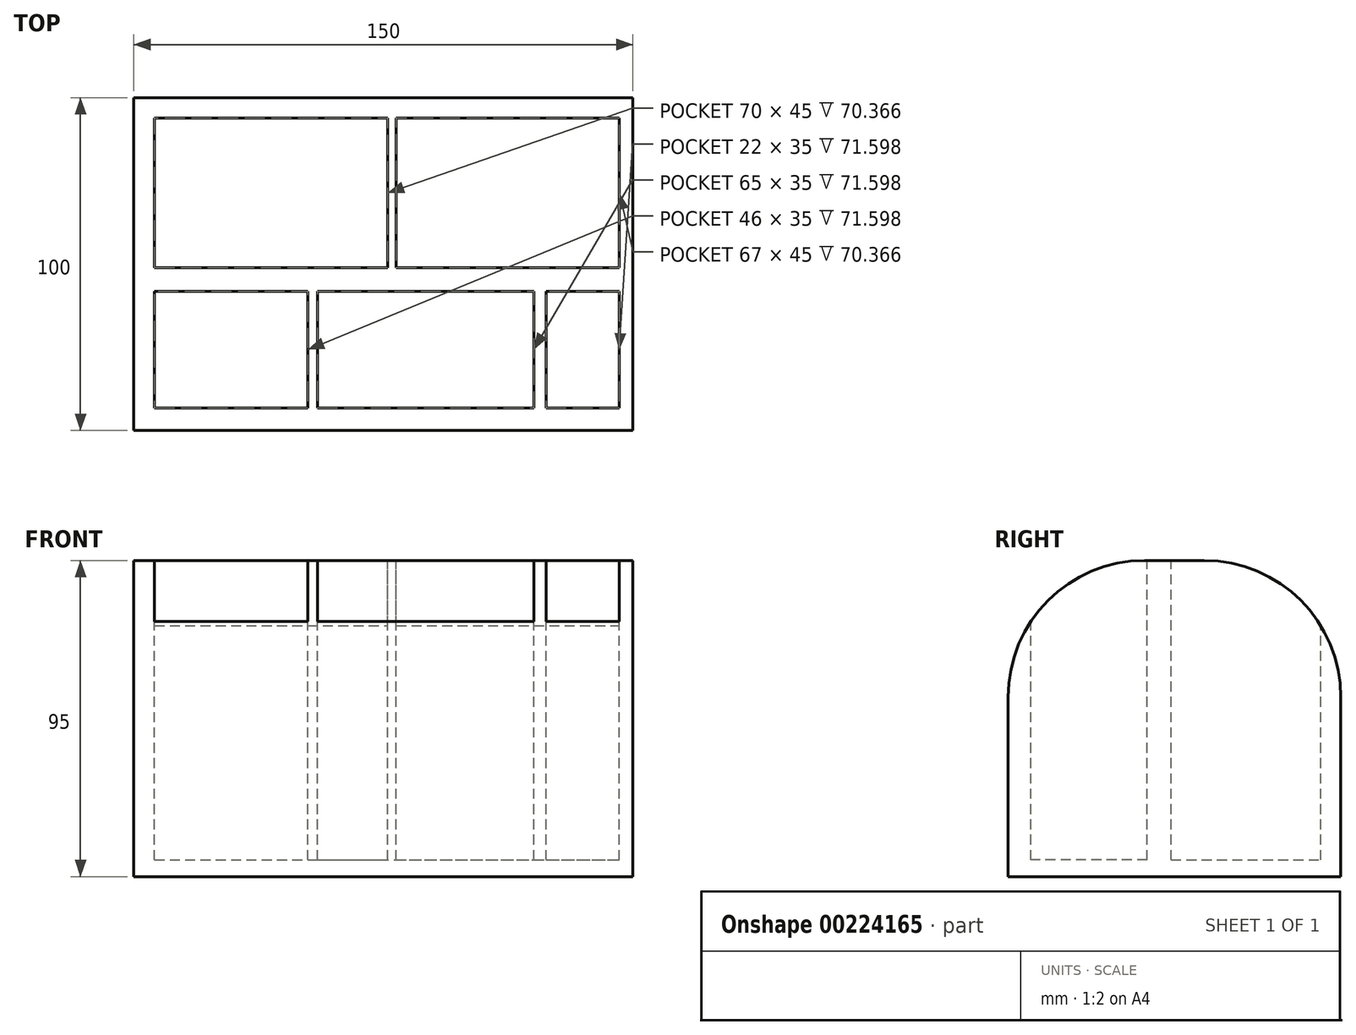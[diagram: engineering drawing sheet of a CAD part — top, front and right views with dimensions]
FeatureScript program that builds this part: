
annotation { "Feature Type Name" : "Feature", "Feature Type Description" : "" }
export const myFeature = defineFeature(function(context is Context, id is Id, definition is map)
    precondition{}
    {
        {
            var Q0;
            Q0=qCreatedBy(makeId("Top.planeOp"),FACE);
            var sketch = newSketch(context, id + "F0", { "sketchPlane" : qUnion([Q0])});
            skLineSegment(sketch, "E0.bottom", {"start": v(-52.23, 53.64) * mm, "end": v(97.77, 53.64) * mm});
            skLineSegment(sketch, "E0.top", {"start": v(-52.23, -46.36) * mm, "end": v(97.77, -46.36) * mm});
            skLineSegment(sketch, "E0.left", {"start": v(-52.23, 53.64) * mm, "end": v(-52.23, -46.36) * mm});
            skLineSegment(sketch, "E0.right", {"start": v(97.77, 53.64) * mm, "end": v(97.77, -46.36) * mm});
            skSolve(sketch);
        }
        {
            var Q0;
            Q0=makeQuery(id+"F0.imprint","IMPRINT",FACE,{"disambiguationData":[TD([[makeQuery(id+"F0.imprint","IMPRINT",EDGE,{"derivedFrom":sQuery(id+"F0.wireOp",EDGE,"E0.bottom")}),-1.0]])]});
            extrude(context, id + "F1", {"entities" : qUnion([Q0]), "depth" : 95 * mm});
        }
        {
            var Q0;
            Q0=makeQuery(id+"F1.opExtrude","CAP_FACE",FACE,{"disambiguationData":[OSD([sQuery(id+"F0.wireOp",EDGE,"E0.bottom"),sQuery(id+"F0.wireOp",EDGE,"E0.top"),sQuery(id+"F0.wireOp",EDGE,"E0.left"),sQuery(id+"F0.wireOp",EDGE,"E0.right")])],"isStart":false});
            var sketch = newSketch(context, id + "F2", { "sketchPlane" : qUnion([Q0])});
            skLineSegment(sketch, "E1.bottom", {"start": v(-46, -39.55) * mm, "end": v(0, -39.55) * mm});
            skLineSegment(sketch, "E1.top", {"start": v(-46, -4.55) * mm, "end": v(0, -4.55) * mm});
            skLineSegment(sketch, "E1.left", {"start": v(-46, -39.55) * mm, "end": v(-46, -4.55) * mm});
            skLineSegment(sketch, "E1.right", {"start": v(0, -39.55) * mm, "end": v(0, -4.55) * mm});
            skLineSegment(sketch, "E2.bottom", {"start": v(2.94, -4.55) * mm, "end": v(67.94, -4.55) * mm});
            skLineSegment(sketch, "E2.top", {"start": v(2.94, -39.55) * mm, "end": v(67.94, -39.55) * mm});
            skLineSegment(sketch, "E2.left", {"start": v(2.94, -4.55) * mm, "end": v(2.94, -39.55) * mm});
            skLineSegment(sketch, "E2.right", {"start": v(67.94, -4.55) * mm, "end": v(67.94, -39.55) * mm});
            skLineSegment(sketch, "E3.bottom", {"start": v(71.64, -4.55) * mm, "end": v(93.64, -4.55) * mm});
            skLineSegment(sketch, "E3.top", {"start": v(71.64, -39.55) * mm, "end": v(93.64, -39.55) * mm});
            skLineSegment(sketch, "E3.left", {"start": v(71.64, -4.55) * mm, "end": v(71.64, -39.55) * mm});
            skLineSegment(sketch, "E3.right", {"start": v(93.64, -4.55) * mm, "end": v(93.64, -39.55) * mm});
            skLineSegment(sketch, "E4.bottom", {"start": v(-46, 2.62) * mm, "end": v(24, 2.62) * mm});
            skLineSegment(sketch, "E4.top", {"start": v(-46, 47.62) * mm, "end": v(24, 47.62) * mm});
            skLineSegment(sketch, "E4.left", {"start": v(-46, 2.62) * mm, "end": v(-46, 47.62) * mm});
            skLineSegment(sketch, "E4.right", {"start": v(24, 2.62) * mm, "end": v(24, 47.62) * mm});
            skLineSegment(sketch, "E5.bottom", {"start": v(26.64, 2.62) * mm, "end": v(93.64, 2.62) * mm});
            skLineSegment(sketch, "E5.top", {"start": v(26.64, 47.62) * mm, "end": v(93.64, 47.62) * mm});
            skLineSegment(sketch, "E5.left", {"start": v(26.64, 2.62) * mm, "end": v(26.64, 47.62) * mm});
            skLineSegment(sketch, "E5.right", {"start": v(93.64, 2.62) * mm, "end": v(93.64, 47.62) * mm});
            skSolve(sketch);
        }
        {
            var Q0;
            Q0=makeQuery(id+"F2.imprint","IMPRINT",FACE,{"disambiguationData":[TD([[makeQuery(id+"F2.imprint","IMPRINT",EDGE,{"derivedFrom":sQuery(id+"F2.wireOp",EDGE,"E4.bottom")}),1.0]])]});
            var Q1;
            Q1=makeQuery(id+"F2.imprint","IMPRINT",FACE,{"disambiguationData":[TD([[makeQuery(id+"F2.imprint","IMPRINT",EDGE,{"derivedFrom":sQuery(id+"F2.wireOp",EDGE,"E5.bottom")}),1.0]])]});
            var Q2;
            Q2=makeQuery(id+"F2.imprint","IMPRINT",FACE,{"disambiguationData":[TD([[makeQuery(id+"F2.imprint","IMPRINT",EDGE,{"derivedFrom":sQuery(id+"F2.wireOp",EDGE,"E1.bottom")}),1.0]])]});
            var Q3;
            Q3=makeQuery(id+"F2.imprint","IMPRINT",FACE,{"disambiguationData":[TD([[makeQuery(id+"F2.imprint","IMPRINT",EDGE,{"derivedFrom":sQuery(id+"F2.wireOp",EDGE,"E2.bottom")}),-1.0]])]});
            var Q4;
            Q4=makeQuery(id+"F2.imprint","IMPRINT",FACE,{"disambiguationData":[TD([[makeQuery(id+"F2.imprint","IMPRINT",EDGE,{"derivedFrom":sQuery(id+"F2.wireOp",EDGE,"E3.bottom")}),-1.0]])]});
            extrude(context, id + "F3", {"entities" : qUnion([Q0, Q1, Q2, Q3, Q4]), "operationType" : NewBodyOperationType.REMOVE, "oppositeDirection" : true, "depth" : 90 * mm});
        }
        {
            var Q0;
            Q0=makeQuery(id+"F1.opExtrude","CAP_EDGE",EDGE,{"disambiguationData":[OSD([sQuery(id+"F0.wireOp",EDGE,"E0.top")])],"isStart":false});
            var Q1;
            Q1=makeQuery(id+"F1.opExtrude","CAP_EDGE",EDGE,{"disambiguationData":[OSD([sQuery(id+"F0.wireOp",EDGE,"E0.bottom")])],"isStart":false});
            fillet(context, id + "F4", {"entities" : qUnion([Q0, Q1]), "radius" : 41.04 * mm, "tangentPropagation" : true, "allowEdgeOverflow" : false});
        }
    });
